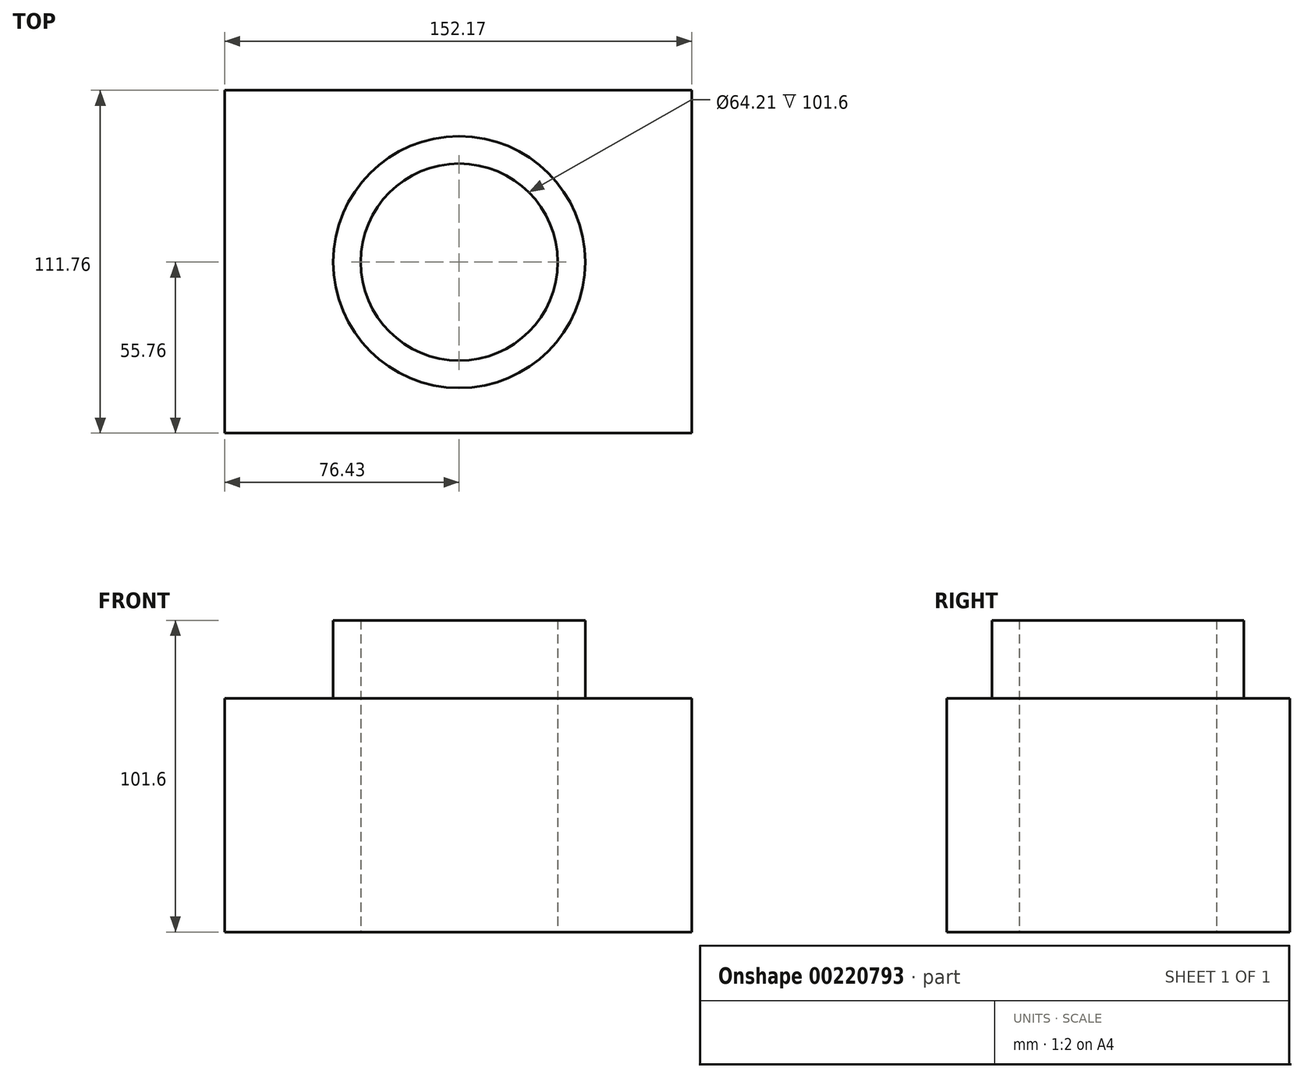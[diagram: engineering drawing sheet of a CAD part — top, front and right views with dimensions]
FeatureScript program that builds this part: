
annotation { "Feature Type Name" : "Feature", "Feature Type Description" : "" }
export const myFeature = defineFeature(function(context is Context, id is Id, definition is map)
    precondition{}
    {
        {
            var Q0;
            Q0=qCreatedBy(makeId("Top.planeOp"),FACE);
            var sketch = newSketch(context, id + "F0", { "sketchPlane" : qUnion([Q0])});
            skLineSegment(sketch, "E0.bottom", {"start": v(-76.43, 56) * mm, "end": v(75.74, 56) * mm});
            skLineSegment(sketch, "E0.top", {"start": v(-76.43, -55.76) * mm, "end": v(75.74, -55.76) * mm});
            skLineSegment(sketch, "E0.left", {"start": v(-76.43, 56) * mm, "end": v(-76.43, -55.76) * mm});
            skLineSegment(sketch, "E0.right", {"start": v(75.74, 56) * mm, "end": v(75.74, -55.76) * mm});
            skCircle(sketch, "E1", {"center": v(0, 0) * mm, "radius": 32.1 * mm});
            skCircle(sketch, "E2", {"center": v(0, 0) * mm, "radius": 41.04 * mm});
            skSolve(sketch);
        }
        {
            var Q0;
            Q0=makeQuery(id+"F0.imprint","IMPRINT",FACE,{"disambiguationData":[TD([[makeQuery(id+"F0.imprint","IMPRINT",EDGE,{"derivedFrom":sQuery(id+"F0.wireOp",EDGE,"E1")}),-1.0]])]});
            extrude(context, id + "F1", {"entities" : qUnion([Q0]), "depth" : 101.6 * mm});
        }
        {
            var Q0;
            Q0 = qSketchRegion(id + "F0", true);
            extrude(context, id + "F2", {"entities" : qUnion([Q0]), "operationType" : NewBodyOperationType.ADD, "depth" : 76.2 * mm});
        }
    });
